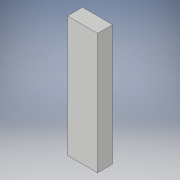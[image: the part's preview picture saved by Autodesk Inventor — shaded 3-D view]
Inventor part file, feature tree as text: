
AUTODESK INVENTOR PART (.ipt)
format: ipt  version: 2017 (Build 210142000, 142)  size: 89,088 bytes
history: native  units: in
note: dims shown in document units (in); Inventor stores cm internally (conversion verified against a paired STEP export)
features: extrude x1, sketch x1
ambient origin geometry x8: Origin, YZ Plane, XZ Plane, XY Plane, X Axis, Y Axis, Z Axis, Center Point
bodies: Solid1 (feature_tree)
feature tree (2):
  extrude  "Extrusion1"  Depth=24.0in
  sketch  "Sketch1"  dims[d0=6.0in d1=24.0in d2=3.0in d3=0.0in]
